# Revit family: Core_barstul
name_source: partatom
category: Мебель
revit_build: Autodesk Revit 2017 (Build: 20160225_1515(x64)
units: mm (PartAtom-declared; Revit-internal decimal feet)

## family parameters
Всегда вертикально = Да
Заголовок OmniClass = General Furniture and Specialties
На основе рабочей плоскости = Нет
Номер OmniClass = 23.40.20.00
Общий = Нет
При загрузке вырезать с полостями = Нет
Точка расчета площади = Нет

## types (2) — shared parameters
Back Support = Skandiform Wood Oak
Chair Legs = Skandiform Chrome
Chair Seat = Skandiform Fabric
Depth = 470 мм
Height 1 = 330 мм
Leg Radius = 9 мм
Width = 490 мм
Изготовитель = Skandiform AB
Ключевая пометка = XBF.2
Комментарии к типоразмеру = Created by Astacus AB
Описание = Stackable bar stool with seat in black or red PUR, back in laminated birch or oak.
Chassis in chromium or silver lacquered metal.

## per-type parameters (varying)
| type | Height | Leg Rad | Seat Height | URL |
| S-070 | 1040 мм | 6 мм | 780 мм | http://file-system.ru |
| S-071 | 910 мм | 5 мм | 650 мм | http://www.biminfo.se |

note: column(s) folded — value = type name in every type: Группа модели

## geometry (parser evidence)
native form markers: Sweep x2
no freeform markers — native parametric forms only
